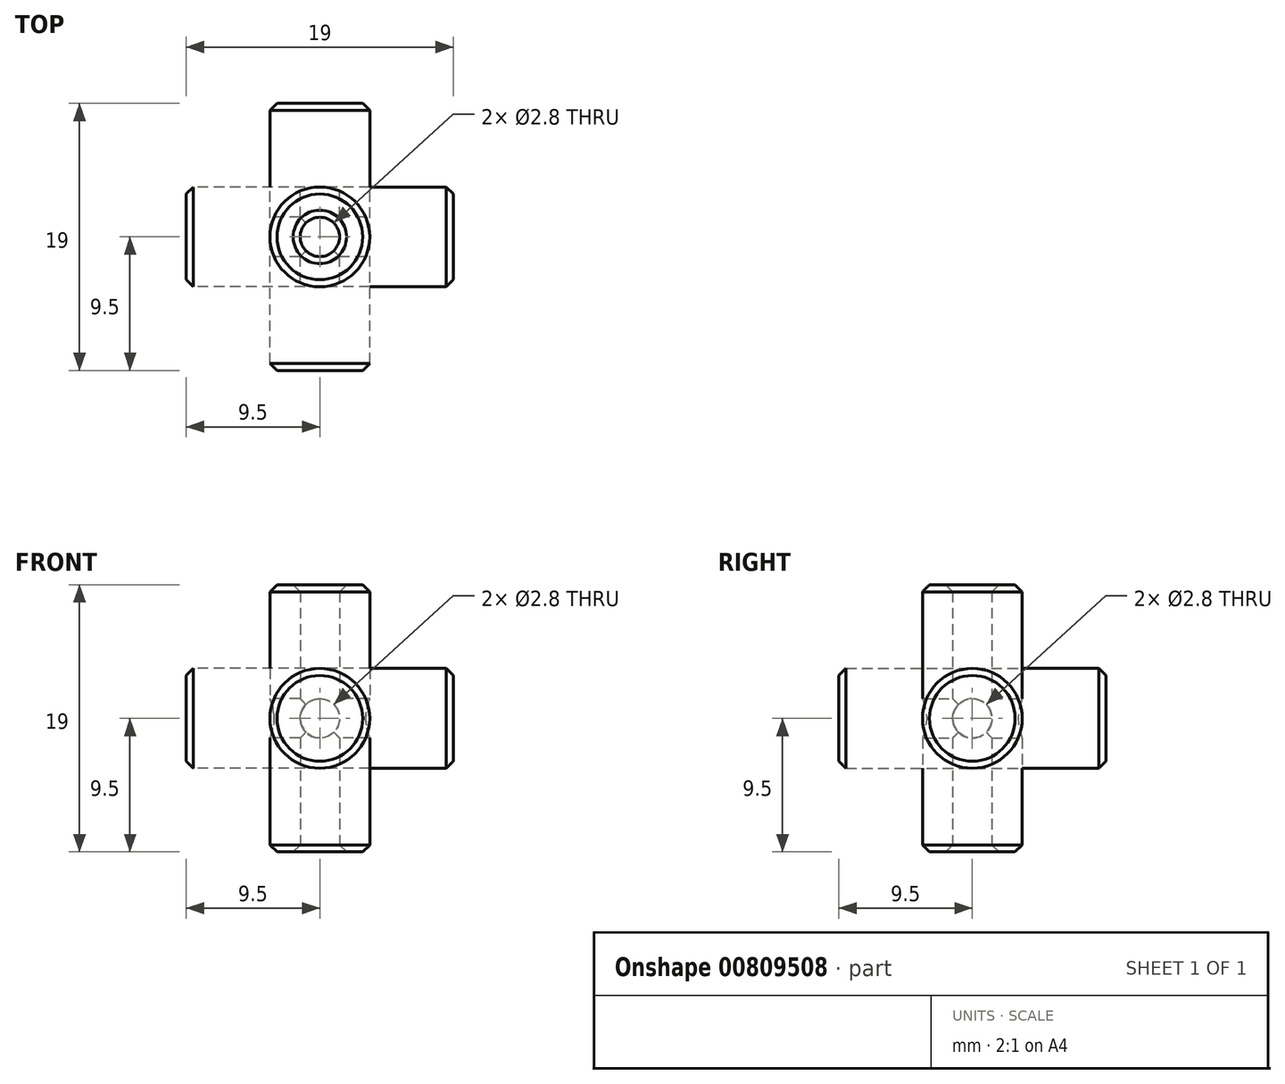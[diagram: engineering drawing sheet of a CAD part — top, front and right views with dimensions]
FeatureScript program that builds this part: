
annotation { "Feature Type Name" : "Feature", "Feature Type Description" : "" }
export const myFeature = defineFeature(function(context is Context, id is Id, definition is map)
    precondition{}
    {
        {
            var Q0;
            Q0=qCreatedBy(makeId("Front.planeOp"),FACE);
            var sketch = newSketch(context, id + "F0", { "sketchPlane" : qUnion([Q0])});
            skCircle(sketch, "E0", {"center": v(0, 0) * mm, "radius": 3.55 * mm});
            skSolve(sketch);
        }
        {
            var Q0;
            Q0=makeQuery(id+"F0.imprint","IMPRINT",FACE,{"disambiguationData":[TD([[makeQuery(id+"F0.imprint","IMPRINT",EDGE,{"derivedFrom":sQuery(id+"F0.wireOp",EDGE,"E0")}),1.0]])]});
            extrude(context, id + "F1", {"entities" : qUnion([Q0]), "endBound" : BoundingType.SYMMETRIC, "depth" : 19 * mm, "offsetDistance" : 25 * mm});
        }
        {
            var Q0;
            Q0=qCreatedBy(makeId("Front.planeOp"),FACE);
            var sketch = newSketch(context, id + "F2", { "sketchPlane" : qUnion([Q0])});
            skCircle(sketch, "E1", {"center": v(0, 0) * mm, "radius": 1.4 * mm});
            skSolve(sketch);
        }
        {
            var Q0;
            Q0 = qSketchRegion(id + "F2", true);
            extrude(context, id + "F3", {"entities" : qUnion([Q0]), "endBound" : BoundingType.SYMMETRIC, "depth" : 20 * mm, "offsetDistance" : 25 * mm});
        }
        {
            var Q0;
            Q0=qCreatedBy(makeId("Front.planeOp"),FACE);
            var sketch = newSketch(context, id + "F4", { "sketchPlane" : qUnion([Q0])});
            skLineSegment(sketch, "E2.bottom", {"start": v(0, 0) * mm, "end": v(10, 0) * mm});
            skLineSegment(sketch, "E2.top", {"start": v(0, 10) * mm, "end": v(10, 10) * mm});
            skLineSegment(sketch, "E2.left", {"start": v(0, 0) * mm, "end": v(0, 10) * mm});
            skLineSegment(sketch, "E2.right", {"start": v(10, 0) * mm, "end": v(10, 10) * mm});
            skSolve(sketch);
        }
        {
            var Q0;
            Q0 = qSketchRegion(id + "F4", true);
            extrude(context, id + "F5", {"entities" : qUnion([Q0]), "depth" : 10 * mm, "offsetDistance" : 25 * mm});
        }
        {
            var Q0;
            Q0=qCreatedBy(makeId("Origin.pointOp"),VERTEX);
            var Q1;
            Q1=makeQuery(id+"F5.opExtrude","CAP_VERTEX",VERTEX,{"disambiguationData":[OSD([sQuery(id+"F4.wireOp",EDGE,"E2.top"),sQuery(id+"F4.wireOp",EDGE,"E2.right")])],"isStart":false});
            var Q2;
            Q2=makeQuery(id+"F5.opExtrude","CAP_VERTEX",VERTEX,{"disambiguationData":[OSD([sQuery(id+"F4.wireOp",EDGE,"E2.bottom"),sQuery(id+"F4.wireOp",EDGE,"E2.right")])],"isStart":false});
            cPlane(context, id + "F6", {"entities" : qUnion([Q0, Q1, Q2]), "cplaneType" : CPlaneType.THREE_POINT, "offset" : 25 * mm, "width" : 150 * mm, "height" : 150 * mm});
        }
        {
            var Q0;
            Q0=qCreatedBy(id+"F6.planeOp",FACE);
            var sketch = newSketch(context, id + "F7", { "sketchPlane" : qUnion([Q0])});
            skLineSegment(sketch, "E3", {"start": v(0, 0) * mm, "end": v(14.14, 10) * mm});
            skSolve(sketch);
        }
        {
            var Q0;
            Q0=makeQuery(id+"F5.opExtrude","SWEPT_BODY",BODY,{"disambiguationData":[OSD([sQuery(id+"F4.wireOp",EDGE,"E2.bottom"),sQuery(id+"F4.wireOp",EDGE,"E2.top"),sQuery(id+"F4.wireOp",EDGE,"E2.left"),sQuery(id+"F4.wireOp",EDGE,"E2.right")])]});
            deleteBodies(context, id + "F8", {"entities" : qUnion([Q0])});
        }
        {
            var Q0;
            Q0=makeQuery(id+"F1.opExtrude","SWEPT_BODY",BODY,{"disambiguationData":[OSD([sQuery(id+"F0.wireOp",EDGE,"E0")])]});
            var Q1;
            Q1=makeQuery(id+"F3.opExtrude","SWEPT_BODY",BODY,{"disambiguationData":[OSD([sQuery(id+"F2.wireOp",EDGE,"E1")])]});
            var Q2;
            Q2=sQuery(id+"F7.wireOp",EDGE,"E3");
            circularPattern(context, id + "F9", {"entities" : qUnion([Q0, Q1]), "axis" : qUnion([Q2]), "angle" : 360 * degree, "instanceCount" : 3, "equalSpace" : true});
        }
        {
            var Q0;
            Q0=makeQuery(id+"F3.opExtrude","SWEPT_BODY",BODY,{"disambiguationData":[OSD([sQuery(id+"F2.wireOp",EDGE,"E1")])]});
            var Q1;
            Q1=makeQuery(id+"F9.opPattern","COPY",BODY,{"derivedFrom":makeQuery(id+"F3.opExtrude","SWEPT_BODY",BODY,{"disambiguationData":[OSD([sQuery(id+"F2.wireOp",EDGE,"E1")])]}),"instanceName":"2"});
            var Q2;
            Q2=makeQuery(id+"F9.opPattern","COPY",BODY,{"derivedFrom":makeQuery(id+"F3.opExtrude","SWEPT_BODY",BODY,{"disambiguationData":[OSD([sQuery(id+"F2.wireOp",EDGE,"E1")])]}),"instanceName":"1"});
            var Q3;
            Q3=makeQuery(id+"F9.opPattern","COPY",BODY,{"derivedFrom":makeQuery(id+"F1.opExtrude","SWEPT_BODY",BODY,{"disambiguationData":[OSD([sQuery(id+"F0.wireOp",EDGE,"E0")])]}),"instanceName":"2"});
            booleanBodies(context, id + "F10", {"operationType" : BooleanOperationType.SUBTRACTION, "tools" : qUnion([Q0, Q1, Q2]), "targets" : qUnion([Q3])});
        }
        {
            var Q0;
            Q0=makeQuery(id+"F9.opPattern","COPY",FACE,{"derivedFrom":makeQuery(id+"F1.opExtrude","CAP_FACE",FACE,{"disambiguationData":[OSD([sQuery(id+"F0.wireOp",EDGE,"E0")])],"isStart":false}),"instanceName":"2"});
            var Q1;
            Q1=makeQuery(id+"F1.opExtrude","CAP_FACE",FACE,{"disambiguationData":[OSD([sQuery(id+"F0.wireOp",EDGE,"E0")])],"isStart":false});
            var Q2;
            Q2=makeQuery(id+"F9.opPattern","COPY",FACE,{"derivedFrom":makeQuery(id+"F1.opExtrude","CAP_FACE",FACE,{"disambiguationData":[OSD([sQuery(id+"F0.wireOp",EDGE,"E0")])],"isStart":true}),"instanceName":"2"});
            var Q3;
            Q3=makeQuery(id+"F1.opExtrude","CAP_FACE",FACE,{"disambiguationData":[OSD([sQuery(id+"F0.wireOp",EDGE,"E0")])],"isStart":true});
            var Q4;
            Q4=makeQuery(id+"F9.opPattern","COPY",FACE,{"derivedFrom":makeQuery(id+"F1.opExtrude","CAP_FACE",FACE,{"disambiguationData":[OSD([sQuery(id+"F0.wireOp",EDGE,"E0")])],"isStart":true}),"instanceName":"1"});
            var Q5;
            Q5=makeQuery(id+"F9.opPattern","COPY",FACE,{"derivedFrom":makeQuery(id+"F1.opExtrude","CAP_FACE",FACE,{"disambiguationData":[OSD([sQuery(id+"F0.wireOp",EDGE,"E0")])],"isStart":false}),"instanceName":"1"});
            chamfer(context, id + "F11", {"entities" : qUnion([Q0, Q1, Q2, Q3, Q4, Q5]), "width" : 0.5 * mm, "tangentPropagation" : true});
        }
    });
